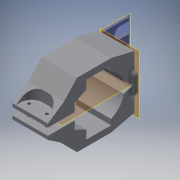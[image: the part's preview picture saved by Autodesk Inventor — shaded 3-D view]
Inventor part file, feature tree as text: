
AUTODESK INVENTOR PART (.ipt)
format: ipt  version: 2016 (Build 200138000, 138)  size: 489,472 bytes
history: native  units: in
note: dims shown in document units (in); Inventor stores cm internally (conversion verified against a paired STEP export)
features: sketch x12, extrude x11, projected_geometry x6, plane x4, reference x4, fillet x3, revolve x1
ambient origin geometry x8: Origin, YZ Plane, XZ Plane, XY Plane, X Axis, Y Axis, Z Axis, Center Point
bodies: Solid1 (feature_tree)
feature tree (41):
  plane  "Work Plane1"
  plane  "Work Plane2"
  extrude  "Extrusion1"  Depth=1.315in
  plane  "Work Plane3"
  extrude  "Extrusion2"  Depth=1.4in
  extrude  "Extrusion3"  Depth=1.8in TaperAngle=0.0deg
  plane  "Work Plane4"
  revolve  "Revolution1"  [1 undecoded]
  fillet  "Fillet1"  Radius=1.925in
  extrude  "Extrusion4"  TaperAngle=90.0deg  [1 undecoded]
  extrude  "Extrusion5"  Depth=0.2in TaperAngle=0.0deg
  extrude  "Extrusion6"  Depth=0.2in TaperAngle=0.0deg
  extrude  "Extrusion7"  Depth=2.575in TaperAngle=0.0deg
  extrude  "Extrusion8"  Depth=0.175in
  extrude  "Extrusion9"  Depth=0.2in TaperAngle=0.0deg
  fillet  "Fillet2"  Radius=0.2in
  fillet  "Fillet3"  Radius=0.625in
  extrude  "Extrusion10"  Depth=0.35in
  extrude  "Extrusion11"  Depth=0.2in
  sketch  "Sketch1"  dims[d2=0.6575in d3=1.315in]
  reference  "Reference1"
  sketch  "Sketch2"  dims[d10=2.92in d11=1.4in]
  sketch  "Sketch3"  dims[d12=0.35in d13=1.8in d14=0.0in]
  reference  "Reference2"
  sketch  "Sketch4"  dims[d15=0.5in d16=0.35in d17=1.925in d18=0.0in]
  reference  "Reference3"
  sketch  "Sketch5"  dims[d19=1.925in d20=0.0in d21=90.0deg]
  projected_geometry  "Projected Loop1"
  reference  "Reference4"
  sketch  "Sketch6"  dims[d22=0.3125in d23=0.2in d24=0.0in]
  projected_geometry  "Projected Loop2"
  sketch  "Sketch7"  dims[d25=1.5in d26=0.2in d27=0.0in]
  projected_geometry  "Projected Loop3"
  sketch  "Sketch8"  dims[d28=0.4in d29=2.575in d30=0.0in]
  projected_geometry  "Projected Loop4"
  sketch  "Sketch9"  dims[d31=0.175in d32=0.175in]
  sketch  "Sketch10"  dims[d33=2.575in d34=0.0in d35=0.2in d36=0.0in d37=0.2in d38=0.0in d39=0.625in]
  sketch  "Sketch11"  dims[d40=0.625in d41=0.35in]
  projected_geometry  "Projected Loop5"
  sketch  "Sketch12"  dims[d44=0.3in d45=0.2in d46=0.2in d47=0.4in d48=90.0deg d49=0.3in d50=10.0in d51=0.0in d52=0.2in d53=0.0in]
  projected_geometry  "Projected Loop6"
note: 2 required parameter values undecoded (feature->parameter linkage not recoverable at this tier; creation-order binding heuristic only, values carry confidence <= 0.55)